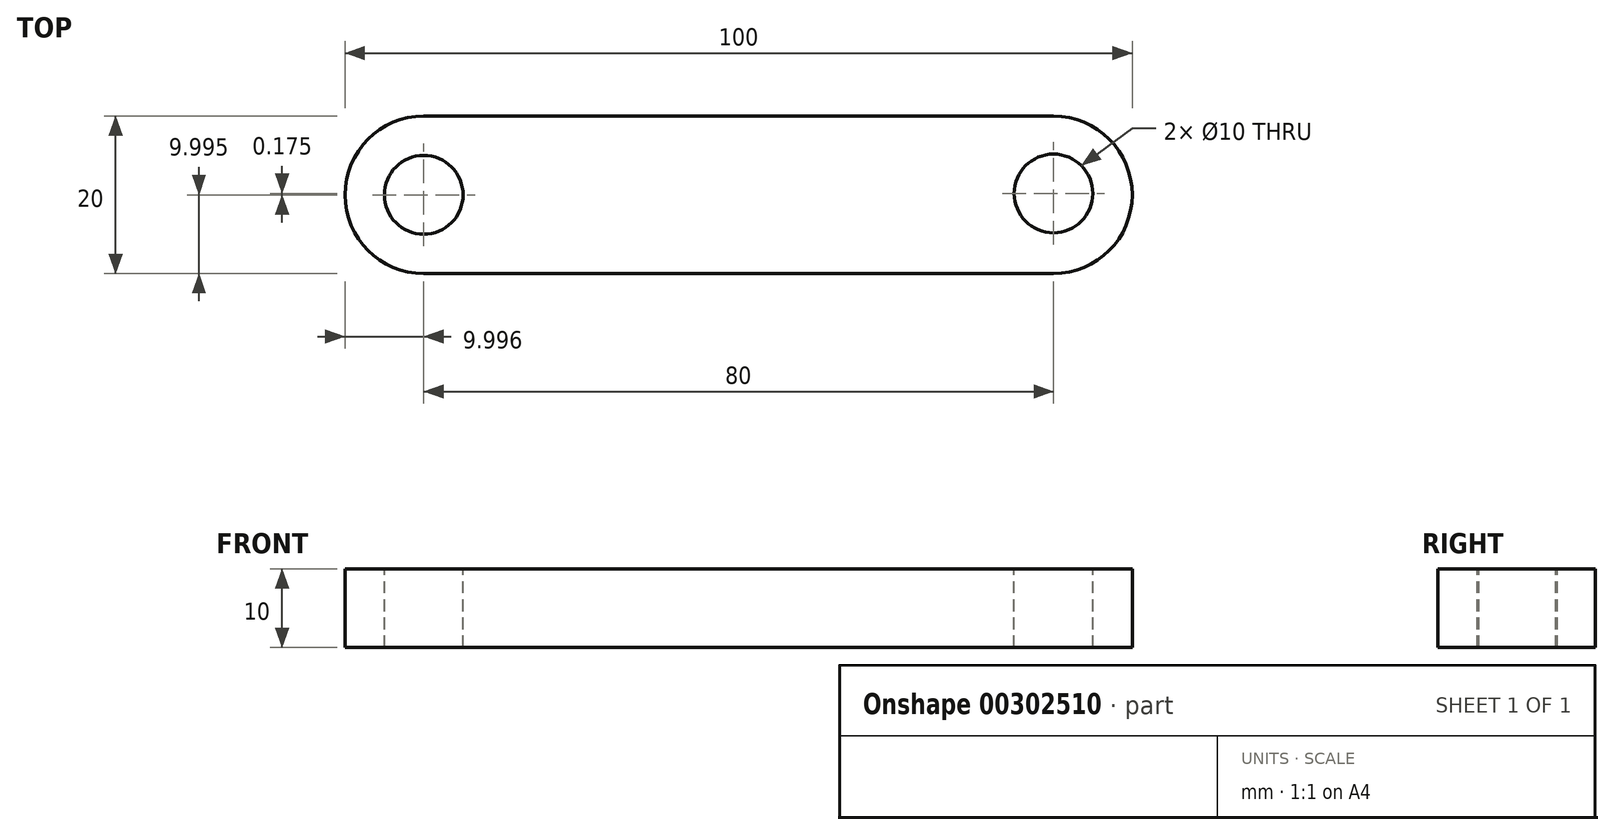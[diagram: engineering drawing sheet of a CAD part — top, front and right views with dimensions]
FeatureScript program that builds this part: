
annotation { "Feature Type Name" : "Feature", "Feature Type Description" : "" }
export const myFeature = defineFeature(function(context is Context, id is Id, definition is map)
    precondition{}
    {
        {
            var Q0;
            Q0=qCreatedBy(makeId("Top.planeOp"),FACE);
            var sketch = newSketch(context, id + "F0", { "sketchPlane" : qUnion([Q0])});
            skLineSegment(sketch, "E0", {"start": v(-33.67, 9.83) * mm, "end": v(46.33, 9.83) * mm});
            skLineSegment(sketch, "E1", {"start": v(-33.67, -10.17) * mm, "end": v(46.33, -10.17) * mm});
            skArc(sketch, "E2", {"start": v(-33.67, 9.83) * mm, "mid": v(-43.67, -0.17) * mm, "end": v(-33.67, -10.17) * mm});
            skArc(sketch, "E3", {"start": v(46.33, -10.17) * mm, "mid": v(56.33, -0.17) * mm, "end": v(46.33, 9.83) * mm});
            skSolve(sketch);
        }
        {
            var Q0;
            Q0 = qSketchRegion(id + "F0", true);
            extrude(context, id + "F1", {"entities" : qUnion([Q0]), "depth" : 10 * mm});
        }
        {
            var Q0;
            Q0=makeQuery(id+"F1.opExtrude","CAP_FACE",FACE,{"disambiguationData":[OSD([sQuery(id+"F0.wireOp",EDGE,"E0"),sQuery(id+"F0.wireOp",EDGE,"E1"),sQuery(id+"F0.wireOp",EDGE,"E2"),sQuery(id+"F0.wireOp",EDGE,"E3")])],"isStart":false});
            var sketch = newSketch(context, id + "F2", { "sketchPlane" : qUnion([Q0])});
            skCircle(sketch, "E4", {"center": v(-33.67, -0.17) * mm, "radius": 5 * mm});
            skCircle(sketch, "E5", {"center": v(46.33, 0) * mm, "radius": 5 * mm});
            skSolve(sketch);
        }
        {
            var Q0;
            Q0 = qSketchRegion(id + "F2", true);
            extrude(context, id + "F3", {"entities" : qUnion([Q0]), "operationType" : NewBodyOperationType.REMOVE, "endBound" : BoundingType.THROUGH_ALL, "oppositeDirection" : true, "depth" : 25 * mm});
        }
    });
